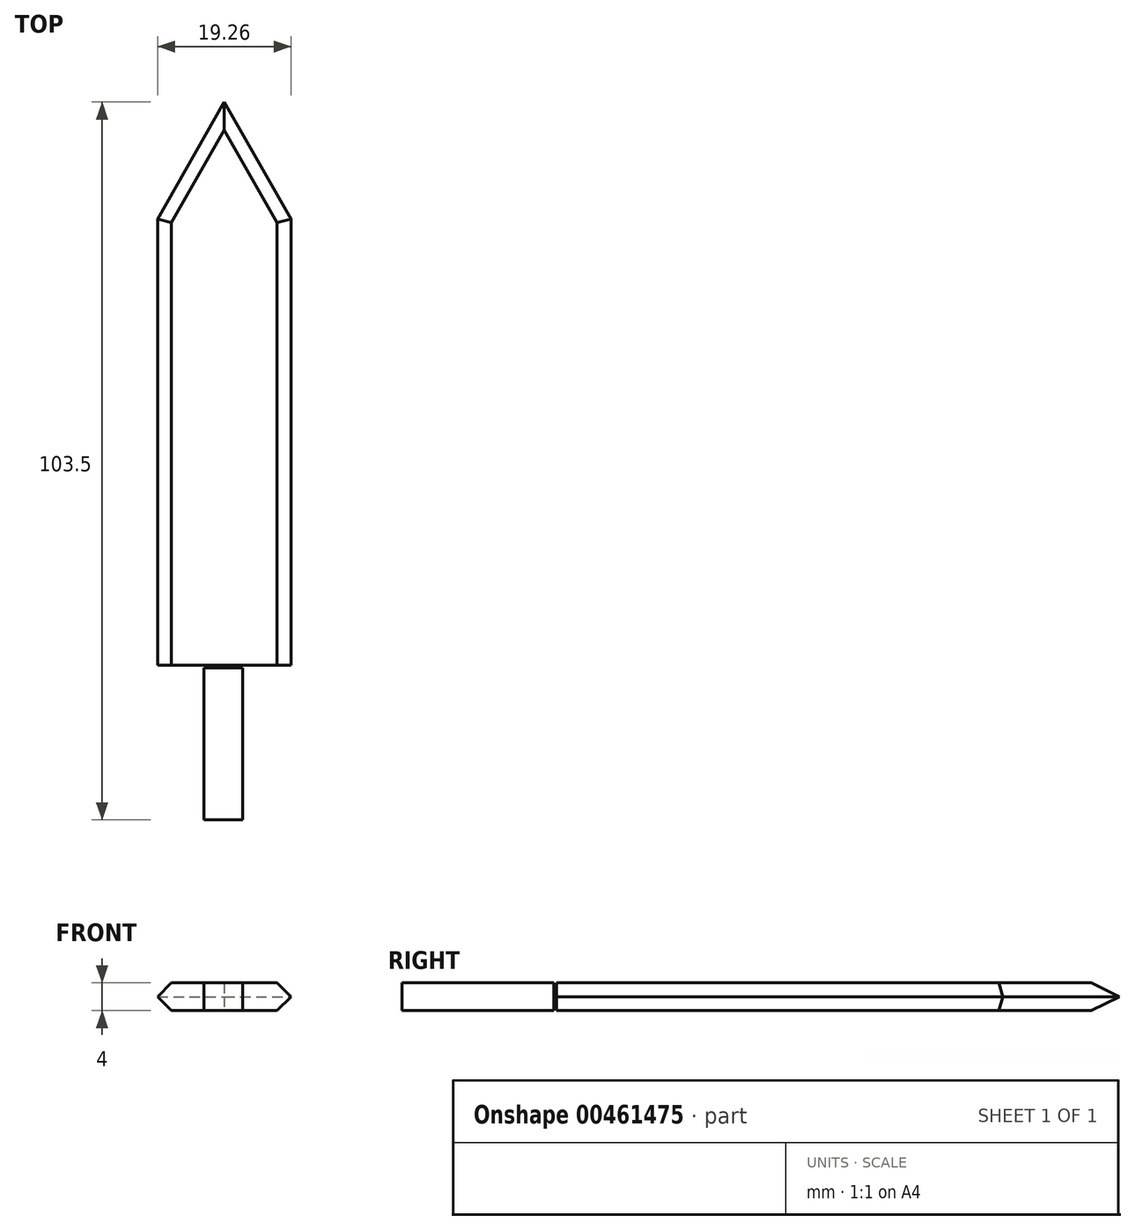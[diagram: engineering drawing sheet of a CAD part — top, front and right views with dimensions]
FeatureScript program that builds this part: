
annotation { "Feature Type Name" : "Feature", "Feature Type Description" : "" }
export const myFeature = defineFeature(function(context is Context, id is Id, definition is map)
    precondition{}
    {
        {
            var Q0;
            Q0=qCreatedBy(makeId("Top.planeOp"),FACE);
            var sketch = newSketch(context, id + "F0", { "sketchPlane" : qUnion([Q0])});
            skLineSegment(sketch, "E0.bottom", {"start": v(-9.63, 32.18) * mm, "end": v(9.63, 32.18) * mm});
            skLineSegment(sketch, "E0.top", {"start": v(-9.63, -32.18) * mm, "end": v(9.63, -32.18) * mm});
            skLineSegment(sketch, "E0.left", {"start": v(-9.63, 32.18) * mm, "end": v(-9.63, -32.18) * mm});
            skLineSegment(sketch, "E0.right", {"start": v(9.63, 32.18) * mm, "end": v(9.63, -32.18) * mm});
            skPoint(sketch, "E0.middle", {"position": v(0, 0) * mm});
            skLineSegment(sketch, "E1", {"start": v(-9.63, 32.18) * mm, "end": v(0, 49.03) * mm});
            skLineSegment(sketch, "E2", {"start": v(9.63, 32.18) * mm, "end": v(0, 49.03) * mm});
            skSolve(sketch);
        }
        {
            var Q0;
            Q0 = qSketchRegion(id + "F0", true);
            extrude(context, id + "F1", {"entities" : qUnion([Q0]), "depth" : 4 * mm});
        }
        {
            var Q0;
            Q0=makeQuery(id+"F1.opExtrude","CAP_EDGE",EDGE,{"disambiguationData":[OSD([sQuery(id+"F0.wireOp",EDGE,"E0.right")])],"isStart":false});
            var Q1;
            Q1=makeQuery(id+"F1.opExtrude","CAP_EDGE",EDGE,{"disambiguationData":[OSD([sQuery(id+"F0.wireOp",EDGE,"E2")])],"isStart":false});
            var Q2;
            Q2=makeQuery(id+"F1.opExtrude","CAP_EDGE",EDGE,{"disambiguationData":[OSD([sQuery(id+"F0.wireOp",EDGE,"E1")])],"isStart":false});
            var Q3;
            Q3=makeQuery(id+"F1.opExtrude","CAP_EDGE",EDGE,{"disambiguationData":[OSD([sQuery(id+"F0.wireOp",EDGE,"E0.left")])],"isStart":false});
            chamfer(context, id + "F2", {"entities" : qUnion([Q0, Q1, Q2, Q3]), "width" : 2 * mm, "tangentPropagation" : true});
        }
        {
            var Q0;
            Q0=makeQuery(id+"F1.opExtrude","CAP_EDGE",EDGE,{"disambiguationData":[OSD([sQuery(id+"F0.wireOp",EDGE,"E2")])],"isStart":true});
            var Q1;
            Q1=makeQuery(id+"F1.opExtrude","CAP_EDGE",EDGE,{"disambiguationData":[OSD([sQuery(id+"F0.wireOp",EDGE,"E1")])],"isStart":true});
            var Q2;
            Q2=makeQuery(id+"F1.opExtrude","CAP_EDGE",EDGE,{"disambiguationData":[OSD([sQuery(id+"F0.wireOp",EDGE,"E0.left")])],"isStart":true});
            var Q3;
            Q3=makeQuery(id+"F1.opExtrude","CAP_EDGE",EDGE,{"disambiguationData":[OSD([sQuery(id+"F0.wireOp",EDGE,"E0.right")])],"isStart":true});
            chamfer(context, id + "F3", {"entities" : qUnion([Q0, Q1, Q2, Q3]), "width" : 2 * mm, "tangentPropagation" : true});
        }
        {
            var Q0;
            Q0=qCreatedBy(makeId("Top.planeOp"),FACE);
            var sketch = newSketch(context, id + "F4", { "sketchPlane" : qUnion([Q0])});
            skLineSegment(sketch, "E3.bottom", {"start": v(-2.96, -32.57) * mm, "end": v(2.66, -32.57) * mm});
            skLineSegment(sketch, "E3.top", {"start": v(-2.96, -54.47) * mm, "end": v(2.66, -54.47) * mm});
            skLineSegment(sketch, "E3.left", {"start": v(-2.96, -32.57) * mm, "end": v(-2.96, -54.47) * mm});
            skLineSegment(sketch, "E3.right", {"start": v(2.66, -32.57) * mm, "end": v(2.66, -54.47) * mm});
            skSolve(sketch);
        }
        {
            var Q0;
            Q0 = qSketchRegion(id + "F4", true);
            extrude(context, id + "F5", {"entities" : qUnion([Q0]), "depth" : 4 * mm});
        }
    });
